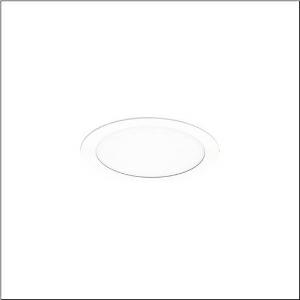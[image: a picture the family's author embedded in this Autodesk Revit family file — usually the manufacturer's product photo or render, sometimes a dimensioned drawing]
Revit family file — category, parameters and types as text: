
# Revit family: lunis_21_l_51db16md91c
name_source: partatom
category: Lighting Fixtures
units: mm (PartAtom-declared; Revit-internal decimal feet)

## family parameters
Cut with Voids When Loaded = No
Host = Face
Light Source = No
Part Type = Normal
Room Calculation Point = No
Round Connector Dimension = Use Diameter
Shared = No

## types (1)
- --- (1 x LED, 3020 lm, 21.7 W, 6500K)
    Apparent Load = 22 VA
    CIE Flux Codes = 50 80 96 100 100
    Color Rendering = 80
    Color Temperature = 6500K
    Default Elevation = 1800 mm
    Description = Lunis 21 L, downlight, light control with lens, of PMMA, optical cover: cover panel, of PC, opal, light emission: direct distribution, LED rated luminous flux: 1.750lm, light colour: 830/840/865, with terminal, 3-pole, mains connection: 220..240V, AC/DC, 0/50..60Hz, housing, round, of diecast aluminium, traffic white (RAL 9016), diameter: 165mm, clamping range: 1..40mm, protection rating (complete): IP20, protection rating (on room side): IP54, insulation class (complete): insulation class II (safety insulation), certification: CE, impact resistance: IK03, packaging unit: 1 piece
    Height = 0 mm  [stored 0 ft]
    Lamp = 1 x LED
    Lamp Light Flux = 3020 lm
    Lamp Power = 21.7 W
    Lamp count = 1
    Length = 165 mm
    Luminous efficacy = 139 lm/W
    Manufacturer = Siteco
    ModVariant = No
    Model = 51DB16MD91C
    Mounting Place = Ceiling
    Mounting Type = Recessed
    Number of Poles = 1
    OnlyDefault = Yes
    Power Factor = 1
    Product Name = Lunis 21 L
    Product group = downlight
    ProductGroupID = 401
    Protection Class = Protection class II
    Protection Degree = IP 20
    RLX_Detail_Level = 1
    RLX_Emergency_Light_Flux = 0 lm
    RLX_Emergency_Type = 0
    RLX_Emergency_Type_DB = No
    RlxData = <blob elided: 13713 chars, md5=735cc20b>
    Socket = socket
    Standby Power = 0 W
    System Light Flux = 3020 lm
    System Power = 22 W
    Type Comments = individual setting: colour temperature 6500K, luminous flux: 100 % | (OFF | ON | ON | ON) | 650 mA
    Type Image = l_1291165.jpg
    URL = http://relux.com
    VarID = @adj_036867
    Voltage = 0 V
    Weight = 0.00 kg
    Width = 0 mm  [stored 0 ft]

note: [stored X ft] marks values corroborated as IEEE doubles in the binary element streams (Revit-internal decimal feet)

## geometry (parser evidence)
native form markers: Sweep x10
no freeform markers — native parametric forms only
